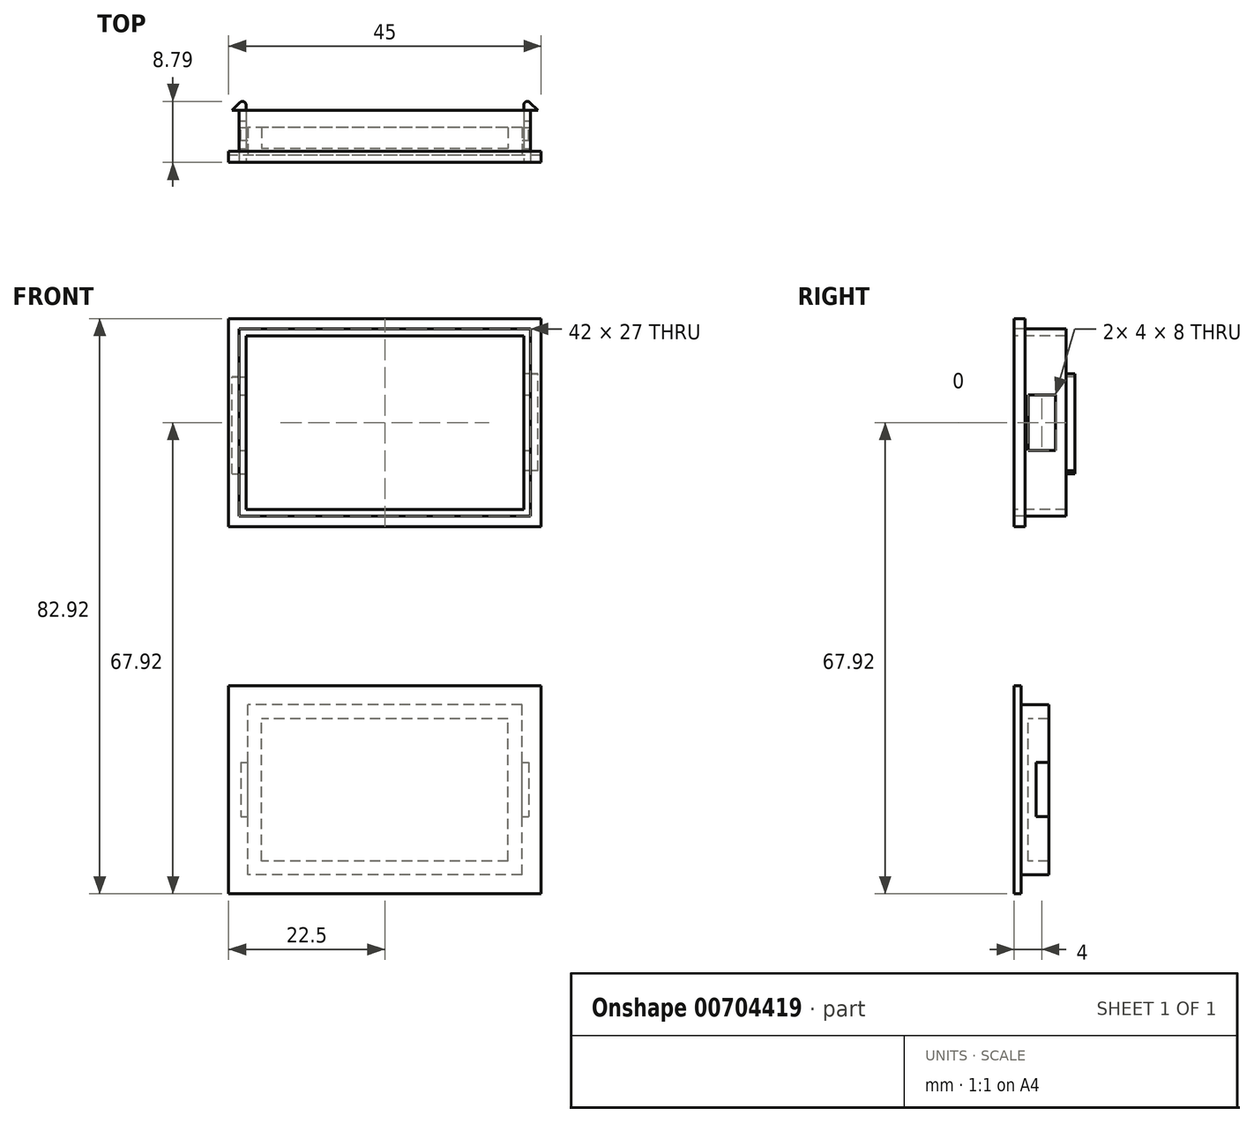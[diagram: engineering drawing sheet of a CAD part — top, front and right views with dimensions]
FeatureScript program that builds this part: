
annotation { "Feature Type Name" : "Feature", "Feature Type Description" : "" }
export const myFeature = defineFeature(function(context is Context, id is Id, definition is map)
    precondition{}
    {
        {
            var Q0;
            Q0=qCreatedBy(makeId("Front.planeOp"),FACE);
            var sketch = newSketch(context, id + "F0", { "sketchPlane" : qUnion([Q0])});
            skLineSegment(sketch, "E0.bottom", {"start": v(20, -12.5) * mm, "end": v(-20, -12.5) * mm});
            skLineSegment(sketch, "E0.top", {"start": v(20, 12.5) * mm, "end": v(-20, 12.5) * mm});
            skLineSegment(sketch, "E0.left", {"start": v(20, -12.5) * mm, "end": v(20, 12.5) * mm});
            skLineSegment(sketch, "E0.right", {"start": v(-20, -12.5) * mm, "end": v(-20, 12.5) * mm});
            skPoint(sketch, "E0.middle", {"position": v(0, 0) * mm});
            skLineSegment(sketch, "E1.bottom", {"start": v(21, -13.5) * mm, "end": v(-21, -13.5) * mm});
            skLineSegment(sketch, "E1.top", {"start": v(21, 13.5) * mm, "end": v(-21, 13.5) * mm});
            skLineSegment(sketch, "E1.left", {"start": v(21, -13.5) * mm, "end": v(21, 13.5) * mm});
            skLineSegment(sketch, "E1.right", {"start": v(-21, -13.5) * mm, "end": v(-21, 13.5) * mm});
            skLineSegment(sketch, "E2.bottom", {"start": v(-22.5, -15) * mm, "end": v(22.5, -15) * mm});
            skLineSegment(sketch, "E2.top", {"start": v(-22.5, 15) * mm, "end": v(22.5, 15) * mm});
            skLineSegment(sketch, "E2.left", {"start": v(-22.5, -15) * mm, "end": v(-22.5, 15) * mm});
            skLineSegment(sketch, "E2.right", {"start": v(22.5, -15) * mm, "end": v(22.5, 15) * mm});
            skLineSegment(sketch, "E3.bottom", {"start": v(22.5, -67.92) * mm, "end": v(-22.5, -67.92) * mm});
            skLineSegment(sketch, "E3.top", {"start": v(22.5, -37.92) * mm, "end": v(-22.5, -37.92) * mm});
            skLineSegment(sketch, "E3.left", {"start": v(22.5, -67.92) * mm, "end": v(22.5, -37.92) * mm});
            skLineSegment(sketch, "E3.right", {"start": v(-22.5, -67.92) * mm, "end": v(-22.5, -37.92) * mm});
            skPoint(sketch, "E3.middle", {"position": v(0, -52.92) * mm});
            skLineSegment(sketch, "E4.bottom", {"start": v(19.75, -65.17) * mm, "end": v(-19.75, -65.17) * mm});
            skLineSegment(sketch, "E4.top", {"start": v(19.75, -40.67) * mm, "end": v(-19.75, -40.67) * mm});
            skLineSegment(sketch, "E4.left", {"start": v(19.75, -65.17) * mm, "end": v(19.75, -40.67) * mm});
            skLineSegment(sketch, "E4.right", {"start": v(-19.75, -65.17) * mm, "end": v(-19.75, -40.67) * mm});
            skSolve(sketch);
        }
        {
            var Q0;
            Q0=makeQuery(id+"F0.imprint","IMPRINT",FACE,{"disambiguationData":[TD([[makeQuery(id+"F0.imprint","IMPRINT",EDGE,{"derivedFrom":sQuery(id+"F0.wireOp",EDGE,"E1.bottom")}),-1.0]])]});
            extrude(context, id + "F1", {"entities" : qUnion([Q0]), "oppositeDirection" : true, "depth" : 7.5 * mm, "offsetDistance" : 25 * mm});
        }
        {
            var Q0;
            Q0=makeQuery(id+"F1.opExtrude","CAP_FACE",FACE,{"disambiguationData":[OSD([sQuery(id+"F0.wireOp",EDGE,"E1.bottom"),sQuery(id+"F0.wireOp",EDGE,"E1.top"),sQuery(id+"F0.wireOp",EDGE,"E1.left"),sQuery(id+"F0.wireOp",EDGE,"E1.right"),sQuery(id+"F0.wireOp",EDGE,"twegKHTT-DPFR-mR3o-F5wY-tLvNdJjQUzrV.bottom"),sQuery(id+"F0.wireOp",EDGE,"twegKHTT-DPFR-mR3o-F5wY-tLvNdJjQUzrV.top"),sQuery(id+"F0.wireOp",EDGE,"twegKHTT-DPFR-mR3o-F5wY-tLvNdJjQUzrV.left"),sQuery(id+"F0.wireOp",EDGE,"twegKHTT-DPFR-mR3o-F5wY-tLvNdJjQUzrV.right")])],"isStart":false});
            var sketch = newSketch(context, id + "F2", { "sketchPlane" : qUnion([Q0])});
            skLineSegment(sketch, "E5.bottom", {"start": v(22, -7.41) * mm, "end": v(20, -7.41) * mm});
            skLineSegment(sketch, "E5.top", {"start": v(22, 6.59) * mm, "end": v(20, 6.59) * mm});
            skLineSegment(sketch, "E5.left", {"start": v(22, -7.41) * mm, "end": v(22, 6.59) * mm});
            skLineSegment(sketch, "E5.right", {"start": v(20, -7.41) * mm, "end": v(20, 6.59) * mm});
            skLineSegment(sketch, "E6.bottom", {"start": v(-22.03, -6.97) * mm, "end": v(-20.03, -6.97) * mm});
            skLineSegment(sketch, "E6.top", {"start": v(-22.03, 7.03) * mm, "end": v(-20.03, 7.03) * mm});
            skLineSegment(sketch, "E6.left", {"start": v(-22.03, -6.97) * mm, "end": v(-22.03, 7.03) * mm});
            skLineSegment(sketch, "E6.right", {"start": v(-20.03, -6.97) * mm, "end": v(-20.03, 7.03) * mm});
            skSolve(sketch);
        }
        {
            var Q0;
            {var subQ0=sQuery(id+"F2.wireOp",EDGE,"A0IgPQm0-aLxR-boHa-o2Og-ehcnsU4r6Wbw.left");Q0=makeQuery(id+"F2.imprint","IMPRINT",FACE,{"disambiguationData":[TD([[makeQuery(id+"F2.imprint","IMPRINT",EDGE,{"derivedFrom":subQ0}),1.0]])]});}
            var Q1;
            {var subQ0=sQuery(id+"F2.wireOp",EDGE,"A0IgPQm0-aLxR-boHa-o2Og-ehcnsU4r6Wbw.right");Q1=makeQuery(id+"F2.imprint","IMPRINT",FACE,{"disambiguationData":[TD([[makeQuery(id+"F2.imprint","IMPRINT",EDGE,{"derivedFrom":subQ0}),-1.0]])]});}
            var Q2;
            {var subQ0=sQuery(id+"F2.wireOp",EDGE,"DGGsRp38-n83j-ldl7-yy1J-MKOVvx9IHiGL.right");Q2=makeQuery(id+"F2.imprint","IMPRINT",FACE,{"disambiguationData":[TD([[makeQuery(id+"F2.imprint","IMPRINT",EDGE,{"derivedFrom":subQ0}),-1.0]])]});}
            var Q3;
            {var subQ0=sQuery(id+"F2.wireOp",EDGE,"DGGsRp38-n83j-ldl7-yy1J-MKOVvx9IHiGL.left");Q3=makeQuery(id+"F2.imprint","IMPRINT",FACE,{"disambiguationData":[TD([[makeQuery(id+"F2.imprint","IMPRINT",EDGE,{"derivedFrom":subQ0}),1.0]])]});}
            var Q4;
            {var subQ0=sQuery(id+"F2.wireOp",EDGE,"E5.left");Q4=makeQuery(id+"F2.imprint","IMPRINT",FACE,{"disambiguationData":[TD([[makeQuery(id+"F2.imprint","IMPRINT",EDGE,{"derivedFrom":subQ0}),1.0]])]});}
            var Q5;
            {var subQ0=sQuery(id+"F2.wireOp",EDGE,"E5.right");Q5=makeQuery(id+"F2.imprint","IMPRINT",FACE,{"disambiguationData":[TD([[makeQuery(id+"F2.imprint","IMPRINT",EDGE,{"derivedFrom":subQ0}),-1.0]])]});}
            var Q6;
            {var subQ0=sQuery(id+"F2.wireOp",EDGE,"E6.left");Q6=makeQuery(id+"F2.imprint","IMPRINT",FACE,{"disambiguationData":[TD([[makeQuery(id+"F2.imprint","IMPRINT",EDGE,{"derivedFrom":subQ0}),-1.0]])]});}
            var Q7;
            {var subQ0=sQuery(id+"F2.wireOp",EDGE,"E6.right");Q7=makeQuery(id+"F2.imprint","IMPRINT",FACE,{"disambiguationData":[TD([[makeQuery(id+"F2.imprint","IMPRINT",EDGE,{"derivedFrom":subQ0}),1.0]])]});}
            extrude(context, id + "F3", {"entities" : qUnion([Q0, Q1, Q2, Q3, Q4, Q5, Q6, Q7]), "operationType" : NewBodyOperationType.ADD, "depth" : 2 * mm, "offsetDistance" : 25 * mm});
        }
        {
            var Q0;
            Q0=makeQuery(id+"F3.opExtrude","CAP_EDGE",EDGE,{"disambiguationData":[OSD([sQuery(id+"F2.wireOp",EDGE,"A0IgPQm0-aLxR-boHa-o2Og-ehcnsU4r6Wbw.right")])],"isStart":false});
            var Q1;
            Q1=makeQuery(id+"F3.opExtrude","CAP_EDGE",EDGE,{"disambiguationData":[OSD([sQuery(id+"F2.wireOp",EDGE,"DGGsRp38-n83j-ldl7-yy1J-MKOVvx9IHiGL.left")])],"isStart":false});
            var Q2;
            Q2=makeQuery(id+"F3.opExtrude","CAP_EDGE",EDGE,{"disambiguationData":[OSD([sQuery(id+"F2.wireOp",EDGE,"E5.left")])],"isStart":false});
            var Q3;
            Q3=makeQuery(id+"F3.opExtrude","CAP_EDGE",EDGE,{"disambiguationData":[OSD([sQuery(id+"F2.wireOp",EDGE,"E6.left")])],"isStart":false});
            chamfer(context, id + "F4", {"entities" : qUnion([Q0, Q1, Q2, Q3]), "width" : 2 * mm, "tangentPropagation" : true});
        }
        {
            var Q0;
            Q0=makeQuery(id+"F4.opChamfer","BLEND_EDGE",EDGE,{"blendedFrom":[makeQuery(id+"F3.opExtrude","CAP_EDGE",EDGE,{"disambiguationData":[OSD([sQuery(id+"F2.wireOp",EDGE,"A0IgPQm0-aLxR-boHa-o2Og-ehcnsU4r6Wbw.right")])],"isStart":false}),makeQuery(id+"F3.boolean.opBoolean","MERGE",FACE,{"derivedFrom":[makeQuery(id+"F1.opExtrude","SWEPT_FACE",FACE,{"disambiguationData":[OSD([sQuery(id+"F0.wireOp",EDGE,"E1.right")])]}),makeQuery(id+"F3.opExtrude","SWEPT_FACE",FACE,{"disambiguationData":[OSD([sQuery(id+"F2.wireOp",EDGE,"A0IgPQm0-aLxR-boHa-o2Og-ehcnsU4r6Wbw.left")])]})]})],"blendedInto":[makeQuery(id+"F3.boolean.opBoolean","MERGE",FACE,{"derivedFrom":[makeQuery(id+"F1.opExtrude","SWEPT_FACE",FACE,{"disambiguationData":[OSD([sQuery(id+"F0.wireOp",EDGE,"E1.right")])]}),makeQuery(id+"F3.opExtrude","SWEPT_FACE",FACE,{"disambiguationData":[OSD([sQuery(id+"F2.wireOp",EDGE,"A0IgPQm0-aLxR-boHa-o2Og-ehcnsU4r6Wbw.left")])]})]})]});
            var Q1;
            Q1=makeQuery(id+"F4.opChamfer","BLEND_EDGE",EDGE,{"blendedFrom":[makeQuery(id+"F3.opExtrude","CAP_EDGE",EDGE,{"disambiguationData":[OSD([sQuery(id+"F2.wireOp",EDGE,"DGGsRp38-n83j-ldl7-yy1J-MKOVvx9IHiGL.left")])],"isStart":false}),makeQuery(id+"F3.boolean.opBoolean","MERGE",FACE,{"derivedFrom":[makeQuery(id+"F1.opExtrude","SWEPT_FACE",FACE,{"disambiguationData":[OSD([sQuery(id+"F0.wireOp",EDGE,"E1.left")])]}),makeQuery(id+"F3.opExtrude","SWEPT_FACE",FACE,{"disambiguationData":[OSD([sQuery(id+"F2.wireOp",EDGE,"DGGsRp38-n83j-ldl7-yy1J-MKOVvx9IHiGL.right")])]})]})],"blendedInto":[makeQuery(id+"F3.boolean.opBoolean","MERGE",FACE,{"derivedFrom":[makeQuery(id+"F1.opExtrude","SWEPT_FACE",FACE,{"disambiguationData":[OSD([sQuery(id+"F0.wireOp",EDGE,"E1.left")])]}),makeQuery(id+"F3.opExtrude","SWEPT_FACE",FACE,{"disambiguationData":[OSD([sQuery(id+"F2.wireOp",EDGE,"DGGsRp38-n83j-ldl7-yy1J-MKOVvx9IHiGL.right")])]})]})]});
            var Q2;
            Q2=makeQuery(id+"F4.opChamfer","BLEND_EDGE",EDGE,{"blendedFrom":[makeQuery(id+"F3.opExtrude","CAP_EDGE",EDGE,{"disambiguationData":[OSD([sQuery(id+"F2.wireOp",EDGE,"E5.left")])],"isStart":false}),makeQuery(id+"F3.boolean.opBoolean","MERGE",FACE,{"derivedFrom":[makeQuery(id+"F1.opExtrude","SWEPT_FACE",FACE,{"disambiguationData":[OSD([sQuery(id+"F0.wireOp",EDGE,"E0.right")])]}),makeQuery(id+"F3.opExtrude","SWEPT_FACE",FACE,{"disambiguationData":[OSD([sQuery(id+"F2.wireOp",EDGE,"E5.right")])]})]})],"blendedInto":[makeQuery(id+"F3.boolean.opBoolean","MERGE",FACE,{"derivedFrom":[makeQuery(id+"F1.opExtrude","SWEPT_FACE",FACE,{"disambiguationData":[OSD([sQuery(id+"F0.wireOp",EDGE,"E0.right")])]}),makeQuery(id+"F3.opExtrude","SWEPT_FACE",FACE,{"disambiguationData":[OSD([sQuery(id+"F2.wireOp",EDGE,"E5.right")])]})]})]});
            var Q3;
            Q3=makeQuery(id+"F4.opChamfer","BLEND_EDGE",EDGE,{"blendedFrom":[makeQuery(id+"F3.opExtrude","CAP_EDGE",EDGE,{"disambiguationData":[OSD([sQuery(id+"F2.wireOp",EDGE,"E6.left")])],"isStart":false}),makeQuery(id+"F3.opExtrude","SWEPT_FACE",FACE,{"disambiguationData":[OSD([sQuery(id+"F2.wireOp",EDGE,"E6.right")])]})],"blendedInto":[makeQuery(id+"F3.opExtrude","SWEPT_FACE",FACE,{"disambiguationData":[OSD([sQuery(id+"F2.wireOp",EDGE,"E6.right")])]})]});
            fillet(context, id + "F5", {"entities" : qUnion([Q0, Q1, Q2, Q3]), "radius" : .5 * mm, "tangentPropagation" : true, "allowEdgeOverflow" : false});
        }
        {
            var Q0;
            Q0=makeQuery(id+"F0.imprint","IMPRINT",FACE,{"disambiguationData":[TD([[makeQuery(id+"F0.imprint","IMPRINT",EDGE,{"derivedFrom":sQuery(id+"F0.wireOp",EDGE,"E1.bottom")}),1.0]])]});
            extrude(context, id + "F6", {"entities" : qUnion([Q0]), "oppositeDirection" : true, "depth" : 1.6 * mm, "offsetDistance" : 25 * mm});
        }
        {
            var Q0;
            Q0=makeQuery(id+"F1.opExtrude","SWEPT_FACE",FACE,{"disambiguationData":[OSD([sQuery(id+"F0.wireOp",EDGE,"E1.left")])]});
            var sketch = newSketch(context, id + "F7", { "sketchPlane" : qUnion([Q0])});
            skLineSegment(sketch, "E7.bottom", {"start": v(6, 4) * mm, "end": v(2, 4) * mm});
            skLineSegment(sketch, "E7.top", {"start": v(6, -4) * mm, "end": v(2, -4) * mm});
            skLineSegment(sketch, "E7.left", {"start": v(6, 4) * mm, "end": v(6, -4) * mm});
            skLineSegment(sketch, "E7.right", {"start": v(2, 4) * mm, "end": v(2, -4) * mm});
            skPoint(sketch, "E7.middle", {"position": v(4, 0) * mm});
            skSolve(sketch);
        }
        {
            var Q0;
            Q0=makeQuery(id+"F7.imprint","IMPRINT",FACE,{"disambiguationData":[TD([[makeQuery(id+"F7.imprint","IMPRINT",EDGE,{"derivedFrom":sQuery(id+"F7.wireOp",EDGE,"E7.bottom")}),1.0]])]});
            extrude(context, id + "F8", {"entities" : qUnion([Q0]), "operationType" : NewBodyOperationType.REMOVE, "endBound" : BoundingType.THROUGH_ALL, "oppositeDirection" : true, "depth" : 25 * mm, "offsetDistance" : 25 * mm});
        }
        {
            var Q0;
            Q0=makeQuery(id+"F0.imprint","IMPRINT",FACE,{"disambiguationData":[TD([[makeQuery(id+"F0.imprint","IMPRINT",EDGE,{"derivedFrom":sQuery(id+"F0.wireOp",EDGE,"E4.bottom")}),-1.0]])]});
            extrude(context, id + "F9", {"entities" : qUnion([Q0]), "oppositeDirection" : true, "depth" : 5 * mm, "offsetDistance" : 25 * mm});
        }
        {
            var Q0;
            Q0=makeQuery(id+"F9.opExtrude","CAP_FACE",FACE,{"disambiguationData":[OSD([sQuery(id+"F0.wireOp",EDGE,"E4.bottom"),sQuery(id+"F0.wireOp",EDGE,"E4.top"),sQuery(id+"F0.wireOp",EDGE,"E4.left"),sQuery(id+"F0.wireOp",EDGE,"E4.right")])],"isStart":false});
            shell(context, id + "F10", {"entities" : qUnion([Q0]), "thickness" : 2 * mm});
        }
        {
            var Q0;
            Q0=makeQuery(id+"F0.imprint","IMPRINT",FACE,{"disambiguationData":[TD([[makeQuery(id+"F0.imprint","IMPRINT",EDGE,{"derivedFrom":sQuery(id+"F0.wireOp",EDGE,"E3.bottom")}),-1.0]])]});
            extrude(context, id + "F11", {"entities" : qUnion([Q0]), "operationType" : NewBodyOperationType.ADD, "oppositeDirection" : true, "depth" : 1 * mm, "offsetDistance" : 25 * mm});
        }
        {
            var Q0;
            Q0=makeQuery(id+"F9.opExtrude","CAP_FACE",FACE,{"disambiguationData":[OSD([sQuery(id+"F0.wireOp",EDGE,"E4.bottom"),sQuery(id+"F0.wireOp",EDGE,"E4.top"),sQuery(id+"F0.wireOp",EDGE,"E4.left"),sQuery(id+"F0.wireOp",EDGE,"E4.right")])],"isStart":false});
            var sketch = newSketch(context, id + "F12", { "sketchPlane" : qUnion([Q0])});
            skLineSegment(sketch, "E8.bottom", {"start": v(20.75, -48.96) * mm, "end": v(17.75, -48.96) * mm});
            skLineSegment(sketch, "E8.top", {"start": v(20.75, -56.76) * mm, "end": v(17.75, -56.76) * mm});
            skLineSegment(sketch, "E8.left", {"start": v(20.75, -48.96) * mm, "end": v(20.75, -56.76) * mm});
            skLineSegment(sketch, "E8.right", {"start": v(17.75, -48.96) * mm, "end": v(17.75, -56.76) * mm});
            skLineSegment(sketch, "E9.bottom", {"start": v(-17.75, -48.96) * mm, "end": v(-20.75, -48.96) * mm});
            skLineSegment(sketch, "E9.top", {"start": v(-17.75, -56.76) * mm, "end": v(-20.75, -56.76) * mm});
            skLineSegment(sketch, "E9.left", {"start": v(-17.75, -48.96) * mm, "end": v(-17.75, -56.76) * mm});
            skLineSegment(sketch, "E9.right", {"start": v(-20.75, -48.96) * mm, "end": v(-20.75, -56.76) * mm});
            skSolve(sketch);
        }
        {
            var Q0;
            {var subQ0=sQuery(id+"F12.wireOp",EDGE,"E9.left");Q0=makeQuery(id+"F12.imprint","IMPRINT",FACE,{"disambiguationData":[TD([[makeQuery(id+"F12.imprint","IMPRINT",EDGE,{"derivedFrom":subQ0}),1.0]])]});}
            var Q1;
            {var subQ0=sQuery(id+"F12.wireOp",EDGE,"E9.right");Q1=makeQuery(id+"F12.imprint","IMPRINT",FACE,{"disambiguationData":[TD([[makeQuery(id+"F12.imprint","IMPRINT",EDGE,{"derivedFrom":subQ0}),1.0]])]});}
            var Q2;
            {var subQ0=sQuery(id+"F12.wireOp",EDGE,"E8.right");Q2=makeQuery(id+"F12.imprint","IMPRINT",FACE,{"disambiguationData":[TD([[makeQuery(id+"F12.imprint","IMPRINT",EDGE,{"derivedFrom":subQ0}),-1.0]])]});}
            var Q3;
            {var subQ0=sQuery(id+"F12.wireOp",EDGE,"E8.left");Q3=makeQuery(id+"F12.imprint","IMPRINT",FACE,{"disambiguationData":[TD([[makeQuery(id+"F12.imprint","IMPRINT",EDGE,{"derivedFrom":subQ0}),-1.0]])]});}
            extrude(context, id + "F13", {"entities" : qUnion([Q0, Q1, Q2, Q3]), "operationType" : NewBodyOperationType.ADD, "oppositeDirection" : true, "depth" : 1.8 * mm, "offsetDistance" : 25 * mm});
        }
    });
